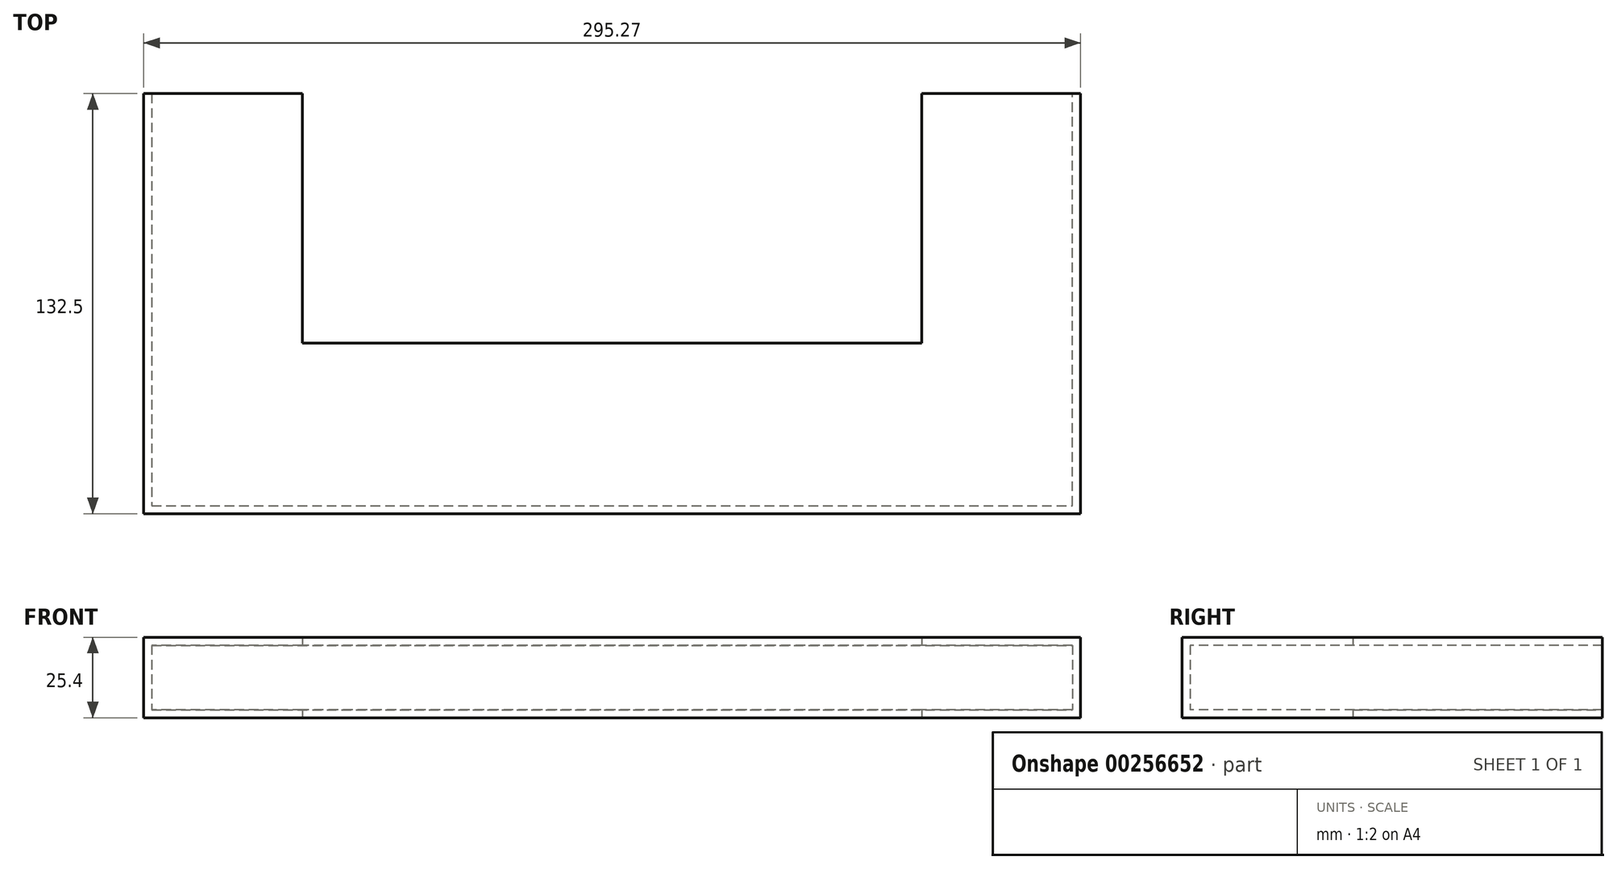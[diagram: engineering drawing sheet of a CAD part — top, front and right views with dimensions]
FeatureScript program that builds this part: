
annotation { "Feature Type Name" : "Feature", "Feature Type Description" : "" }
export const myFeature = defineFeature(function(context is Context, id is Id, definition is map)
    precondition{}
    {
        {
            var Q0;
            Q0=qCreatedBy(makeId("Top.planeOp"),FACE);
            var sketch = newSketch(context, id + "F0", { "sketchPlane" : qUnion([Q0])});
            skLineSegment(sketch, "E0", {"start": v(-140.23, 95.79) * mm, "end": v(-140.23, -36.7) * mm});
            skLineSegment(sketch, "E1", {"start": v(-140.23, -36.7) * mm, "end": v(155.04, -36.7) * mm});
            skLineSegment(sketch, "E2", {"start": v(155.04, -36.7) * mm, "end": v(155.04, 95.79) * mm});
            skLineSegment(sketch, "E3", {"start": v(155.04, 95.79) * mm, "end": v(105.04, 95.79) * mm});
            skLineSegment(sketch, "E4", {"start": v(105.04, 95.79) * mm, "end": v(105.04, 17.15) * mm});
            skLineSegment(sketch, "E5", {"start": v(105.04, 17.15) * mm, "end": v(-90.23, 17.15) * mm});
            skLineSegment(sketch, "E6", {"start": v(-90.23, 17.15) * mm, "end": v(-90.23, 95.79) * mm});
            skLineSegment(sketch, "E7", {"start": v(-90.23, 95.79) * mm, "end": v(-140.23, 95.79) * mm});
            skSolve(sketch);
        }
        {
            var Q0;
            Q0 = qSketchRegion(id + "F0", true);
            extrude(context, id + "F1", {"entities" : qUnion([Q0]), "depth" : 25.4 * mm});
        }
        {
            var Q0;
            Q0=makeQuery(id+"F1.opExtrude","SWEPT_FACE",FACE,{"disambiguationData":[OSD([sQuery(id+"F0.wireOp",EDGE,"E7")])]});
            var Q1;
            Q1=makeQuery(id+"F1.opExtrude","SWEPT_FACE",FACE,{"disambiguationData":[OSD([sQuery(id+"F0.wireOp",EDGE,"E5")])]});
            var Q2;
            Q2=makeQuery(id+"F1.opExtrude","SWEPT_FACE",FACE,{"disambiguationData":[OSD([sQuery(id+"F0.wireOp",EDGE,"E6")])]});
            var Q3;
            Q3=makeQuery(id+"F1.opExtrude","SWEPT_FACE",FACE,{"disambiguationData":[OSD([sQuery(id+"F0.wireOp",EDGE,"E4")])]});
            var Q4;
            Q4=makeQuery(id+"F1.opExtrude","SWEPT_FACE",FACE,{"disambiguationData":[OSD([sQuery(id+"F0.wireOp",EDGE,"E3")])]});
            shell(context, id + "F2", {"entities" : qUnion([Q0, Q1, Q2, Q3, Q4]), "thickness" : 2.54 * mm});
        }
    });
